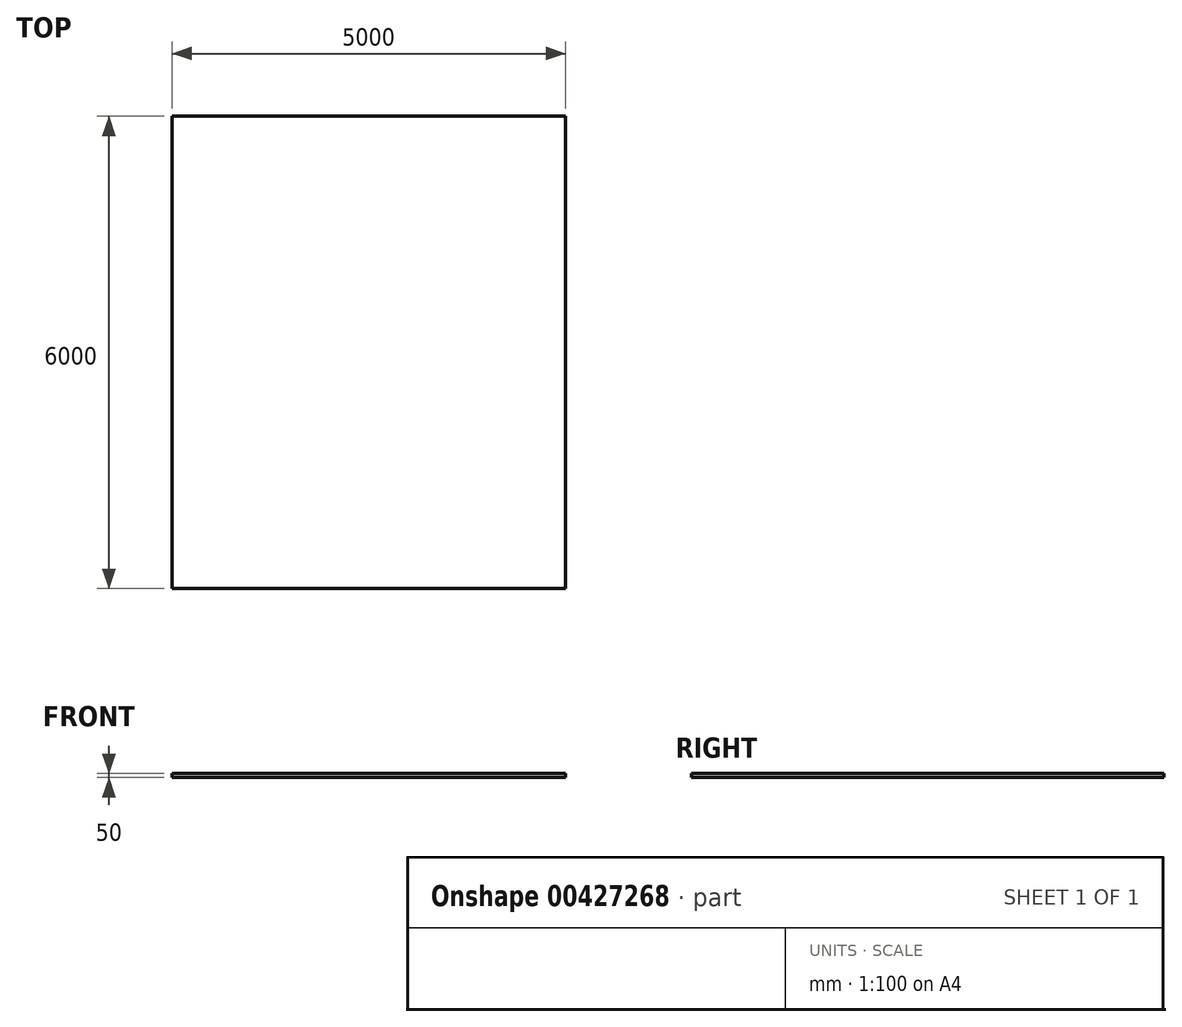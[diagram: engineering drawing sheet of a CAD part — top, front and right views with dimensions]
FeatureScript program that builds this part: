
annotation { "Feature Type Name" : "Feature", "Feature Type Description" : "" }
export const myFeature = defineFeature(function(context is Context, id is Id, definition is map)
    precondition{}
    {
        {
            var Q0;
            Q0=qCreatedBy(makeId("Top.planeOp"),FACE);
            var sketch = newSketch(context, id + "F0", { "sketchPlane" : qUnion([Q0])});
            skLineSegment(sketch, "E0.bottom", {"start": v(0, 0) * mm, "end": v(5000, 0) * mm});
            skLineSegment(sketch, "E0.top", {"start": v(0, 6000) * mm, "end": v(5000, 6000) * mm});
            skLineSegment(sketch, "E0.left", {"start": v(0, 0) * mm, "end": v(0, 6000) * mm});
            skLineSegment(sketch, "E0.right", {"start": v(5000, 0) * mm, "end": v(5000, 6000) * mm});
            skSolve(sketch);
        }
        {
            var Q0;
            Q0=makeQuery(id+"F0.imprint","IMPRINT",FACE,{"disambiguationData":[TD([[makeQuery(id+"F0.imprint","IMPRINT",EDGE,{"derivedFrom":sQuery(id+"F0.wireOp",EDGE,"E0.bottom")}),1.0]])]});
            extrude(context, id + "F1", {"entities" : qUnion([Q0]), "depth" : 50 * mm, "offsetDistance" : 25 * mm});
        }
    });
